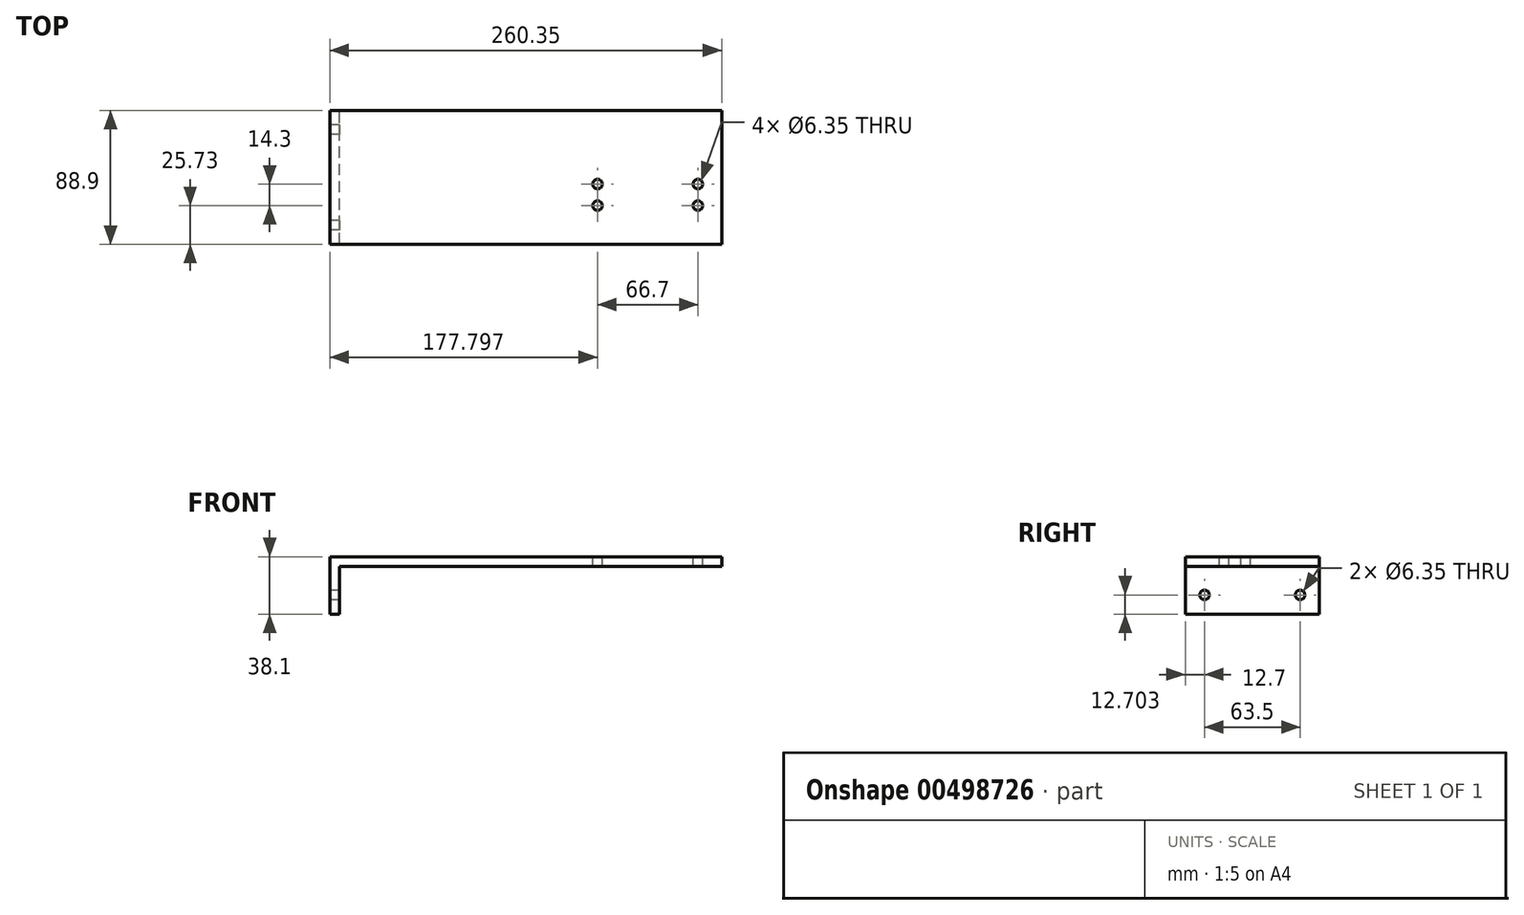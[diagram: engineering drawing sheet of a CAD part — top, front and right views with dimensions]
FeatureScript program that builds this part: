
annotation { "Feature Type Name" : "Feature", "Feature Type Description" : "" }
export const myFeature = defineFeature(function(context is Context, id is Id, definition is map)
    precondition{}
    {
        {
            var Q0;
            Q0=qCreatedBy(makeId("Front.planeOp"),FACE);
            var sketch = newSketch(context, id + "F0", { "sketchPlane" : qUnion([Q0])});
            skLineSegment(sketch, "E0", {"start": v(-57.9, -29.53) * mm, "end": v(-51.54, -29.53) * mm});
            skLineSegment(sketch, "E1", {"start": v(-51.54, -29.53) * mm, "end": v(-51.54, 2.22) * mm});
            skLineSegment(sketch, "E2", {"start": v(-51.54, 2.22) * mm, "end": v(202.46, 2.22) * mm});
            skLineSegment(sketch, "E3", {"start": v(202.46, 2.22) * mm, "end": v(202.46, 8.57) * mm});
            skLineSegment(sketch, "E4", {"start": v(202.46, 8.57) * mm, "end": v(-57.9, 8.57) * mm});
            skLineSegment(sketch, "E5", {"start": v(-57.9, 8.57) * mm, "end": v(-57.9, -29.53) * mm});
            skSolve(sketch);
        }
        {
            var Q0;
            Q0=qSketchRegion(id+"F0",true);
            extrude(context, id + "F1", {"entities" : qUnion([Q0]), "depth" : 88.9 * mm});
        }
        {
            var Q0;
            Q0=makeQuery(id+"F1.opExtrude","SWEPT_FACE",FACE,{"disambiguationData":[OSD([sQuery(id+"F0.wireOp",EDGE,"E4")])]});
            var sketch = newSketch(context, id + "F2", { "sketchPlane" : qUnion([Q0])});
            skCircle(sketch, "E6", {"center": v(119.9, -63.17) * mm, "radius": 3.18 * mm});
            skCircle(sketch, "E7", {"center": v(119.9, -48.87) * mm, "radius": 3.18 * mm});
            skCircle(sketch, "E8", {"center": v(186.6, -63.17) * mm, "radius": 3.18 * mm});
            skCircle(sketch, "E9", {"center": v(186.6, -48.87) * mm, "radius": 3.18 * mm});
            skSolve(sketch);
        }
        {
            var Q0;
            Q0=qSketchRegion(id+"F2",true);
            extrude(context, id + "F3", {"entities" : qUnion([Q0]), "operationType" : NewBodyOperationType.REMOVE, "oppositeDirection" : true, "depth" : 25.4 * mm});
        }
        {
            var Q0;
            Q0=makeQuery(id+"F1.opExtrude","SWEPT_FACE",FACE,{"disambiguationData":[OSD([sQuery(id+"F0.wireOp",EDGE,"E5")])]});
            var sketch = newSketch(context, id + "F4", { "sketchPlane" : qUnion([Q0])});
            skCircle(sketch, "E10", {"center": v(12.7, -16.83) * mm, "radius": 3.18 * mm});
            skCircle(sketch, "E11", {"center": v(76.2, -16.83) * mm, "radius": 3.18 * mm});
            skSolve(sketch);
        }
        {
            var Q0;
            Q0=qSketchRegion(id+"F4",true);
            extrude(context, id + "F5", {"entities" : qUnion([Q0]), "operationType" : NewBodyOperationType.REMOVE, "oppositeDirection" : true, "depth" : 25.4 * mm});
        }
    });
